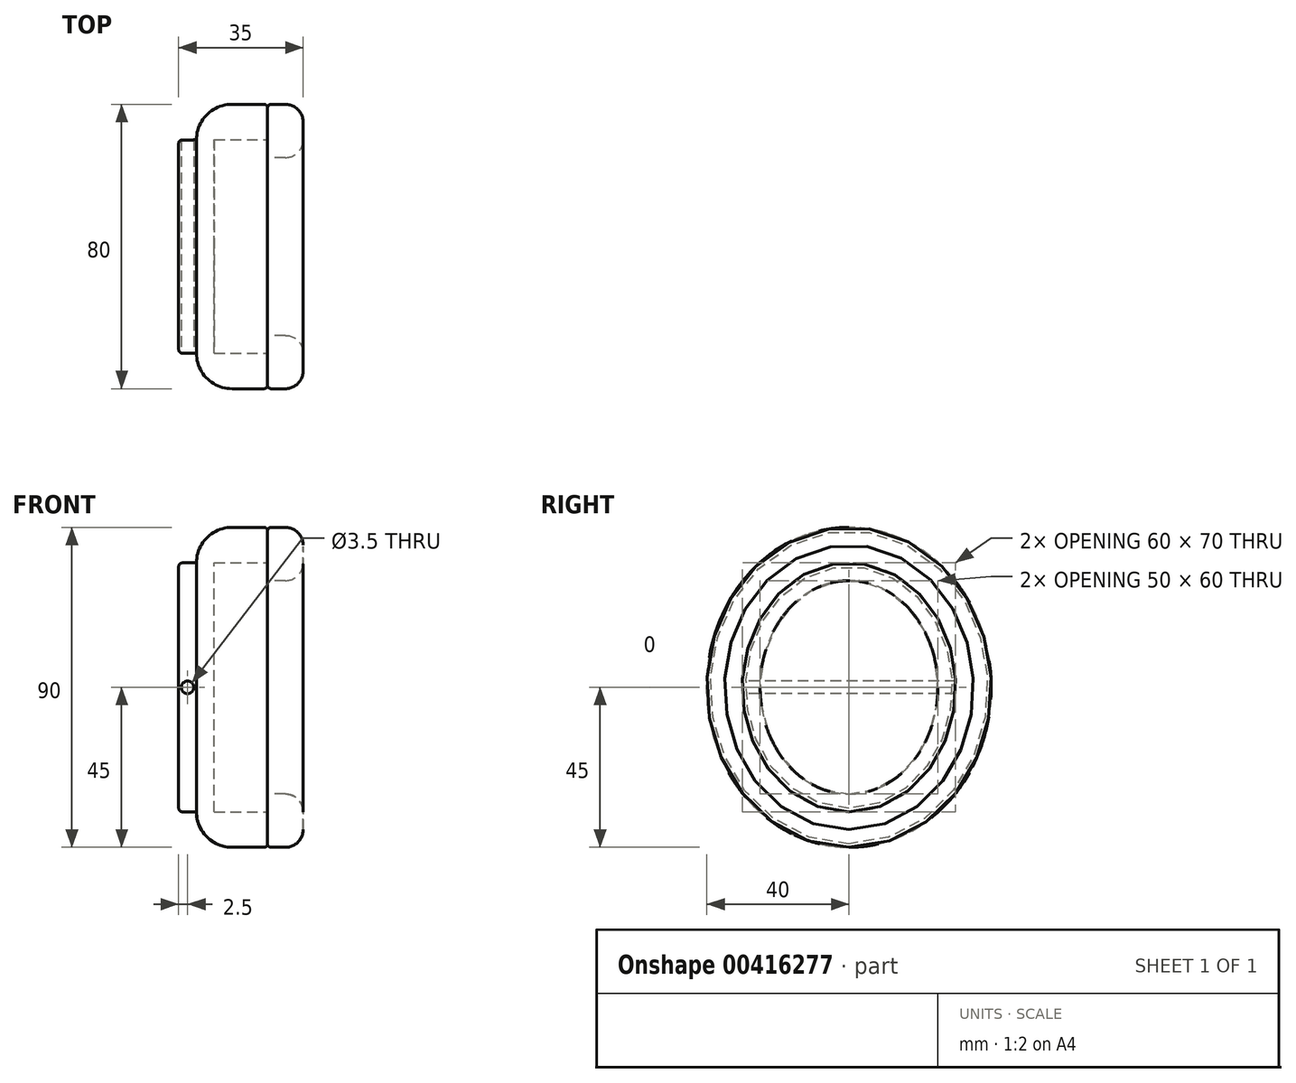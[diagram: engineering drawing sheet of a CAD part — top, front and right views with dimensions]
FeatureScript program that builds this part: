
annotation { "Feature Type Name" : "Feature", "Feature Type Description" : "" }
export const myFeature = defineFeature(function(context is Context, id is Id, definition is map)
    precondition{}
    {
        {
            var Q0;
            Q0=qCreatedBy(makeId("Right.planeOp"),FACE);
            var sketch = newSketch(context, id + "F0", { "sketchPlane" : qUnion([Q0])});
            skEllipse(sketch, "E0", {"center": v(0, 0) * mm, "majorRadius": 35 * mm, "minorRadius": 30 * mm, "majorAxis": v(0, -1)});
            skEllipse(sketch, "E1", {"center": v(0, 0) * mm, "majorRadius": 45 * mm, "minorRadius": 40 * mm, "majorAxis": v(0, -1)});
            skEllipse(sketch, "E2", {"center": v(0, 0) * mm, "majorRadius": 30 * mm, "minorRadius": 25 * mm, "majorAxis": v(0, -1)});
            skSolve(sketch);
        }
        {
            var Q0;
            Q0=makeQuery(id+"F0.imprint","IMPRINT",FACE,{"disambiguationData":[TD([[makeQuery(id+"F0.imprint","IMPRINT",EDGE,{"derivedFrom":sQuery(id+"F0.wireOp",EDGE,"E0")}),1.0]])]});
            var Q1;
            Q1=makeQuery(id+"F0.imprint","IMPRINT",FACE,{"disambiguationData":[TD([[makeQuery(id+"F0.imprint","IMPRINT",EDGE,{"derivedFrom":sQuery(id+"F0.wireOp",EDGE,"E0")}),-1.0]])]});
            var Q2;
            Q2=makeQuery(id+"F0.imprint","IMPRINT",FACE,{"disambiguationData":[TD([[makeQuery(id+"F0.imprint","IMPRINT",EDGE,{"derivedFrom":sQuery(id+"F0.wireOp",EDGE,"E2")}),1.0]])]});
            extrude(context, id + "F1", {"entities" : qUnion([Q0, Q1, Q2]), "oppositeDirection" : true, "depth" : 20 * mm, "offsetDistance" : 25 * mm});
        }
        {
            var Q0;
            Q0=makeQuery(id+"F0.imprint","IMPRINT",FACE,{"disambiguationData":[TD([[makeQuery(id+"F0.imprint","IMPRINT",EDGE,{"derivedFrom":sQuery(id+"F0.wireOp",EDGE,"E0")}),1.0]])]});
            var Q1;
            Q1=makeQuery(id+"F0.imprint","IMPRINT",FACE,{"disambiguationData":[TD([[makeQuery(id+"F0.imprint","IMPRINT",EDGE,{"derivedFrom":sQuery(id+"F0.wireOp",EDGE,"E2")}),1.0]])]});
            extrude(context, id + "F2", {"entities" : qUnion([Q0, Q1]), "operationType" : NewBodyOperationType.REMOVE, "oppositeDirection" : true, "depth" : 15 * mm, "offsetDistance" : 25 * mm});
        }
        {
            var Q0;
            Q0=makeQuery(id+"F0.imprint","IMPRINT",FACE,{"disambiguationData":[TD([[makeQuery(id+"F0.imprint","IMPRINT",EDGE,{"derivedFrom":sQuery(id+"F0.wireOp",EDGE,"E0")}),1.0]])]});
            var Q1;
            Q1=makeQuery(id+"F0.imprint","IMPRINT",FACE,{"disambiguationData":[TD([[makeQuery(id+"F0.imprint","IMPRINT",EDGE,{"derivedFrom":sQuery(id+"F0.wireOp",EDGE,"E0")}),-1.0]])]});
            extrude(context, id + "F3", {"entities" : qUnion([Q0, Q1]), "depth" : 10 * mm, "offsetDistance" : 25 * mm});
        }
        {
            var Q0;
            Q0=makeQuery(id+"F3.opExtrude","CAP_EDGE",EDGE,{"disambiguationData":[OSD([sQuery(id+"F0.wireOp",EDGE,"E1")])],"isStart":false});
            var Q1;
            Q1=makeQuery(id+"F3.opExtrude","CAP_EDGE",EDGE,{"disambiguationData":[OSD([sQuery(id+"F0.wireOp",EDGE,"E2")])],"isStart":false});
            fillet(context, id + "F4", {"entities" : qUnion([Q0, Q1]), "radius" : 5 * mm, "tangentPropagation" : true, "allowEdgeOverflow" : false});
        }
        {
            var Q0;
            Q0=makeQuery(id+"F1.opExtrude","CAP_EDGE",EDGE,{"disambiguationData":[OSD([sQuery(id+"F0.wireOp",EDGE,"E1")])],"isStart":true});
            var Q1;
            Q1=makeQuery(id+"F3.opExtrude","CAP_EDGE",EDGE,{"disambiguationData":[OSD([sQuery(id+"F0.wireOp",EDGE,"E1")])],"isStart":true});
            fillet(context, id + "F5", {"entities" : qUnion([Q0, Q1]), "radius" : 1 * mm, "tangentPropagation" : true, "allowEdgeOverflow" : false});
        }
        {
            var Q0;
            Q0=makeQuery(id+"F1.opExtrude","CAP_EDGE",EDGE,{"disambiguationData":[OSD([sQuery(id+"F0.wireOp",EDGE,"E1")])],"isStart":false});
            fillet(context, id + "F6", {"entities" : qUnion([Q0]), "radius" : 10 * mm, "tangentPropagation" : true, "allowEdgeOverflow" : false});
        }
        {
            var Q0;
            Q0=makeQuery(id+"F1.opExtrude","CAP_FACE",FACE,{"disambiguationData":[OSD([sQuery(id+"F0.wireOp",EDGE,"E1")])],"isStart":false});
            extrude(context, id + "F7", {"entities" : qUnion([Q0]), "operationType" : NewBodyOperationType.ADD, "depth" : 5 * mm, "offsetDistance" : 25 * mm});
        }
        {
            var Q0;
            Q0=qCreatedBy(makeId("Front.planeOp"),FACE);
            var sketch = newSketch(context, id + "F8", { "sketchPlane" : qUnion([Q0])});
            skLineSegment(sketch, "E3", {"start": v(0, 0) * mm, "end": v(-22.5, 0) * mm});
            skCircle(sketch, "E4", {"center": v(-22.5, 0) * mm, "radius": 1.75 * mm});
            skSolve(sketch);
        }
        {
            var Q0;
            Q0=makeQuery(id+"F8.imprint","IMPRINT",FACE,{"disambiguationData":[TD([[makeQuery(id+"F8.imprint","IMPRINT",EDGE,{"derivedFrom":sQuery(id+"F8.wireOp",EDGE,"E4")}),1.0]])]});
            extrude(context, id + "F9", {"entities" : qUnion([Q0]), "operationType" : NewBodyOperationType.REMOVE, "oppositeDirection" : true, "depth" : 60 * mm, "offsetDistance" : 25 * mm, "symmetric" : true});
        }
        {
            var Q0;
            Q0=makeQuery(id+"F7.opExtrude","CAP_EDGE",EDGE,{"disambiguationData":[OSD([sQuery(id+"F0.wireOp",EDGE,"E1")])],"isStart":false});
            fillet(context, id + "F10", {"entities" : qUnion([Q0]), "radius" : 1 * mm, "tangentPropagation" : true, "allowEdgeOverflow" : false});
        }
    });
